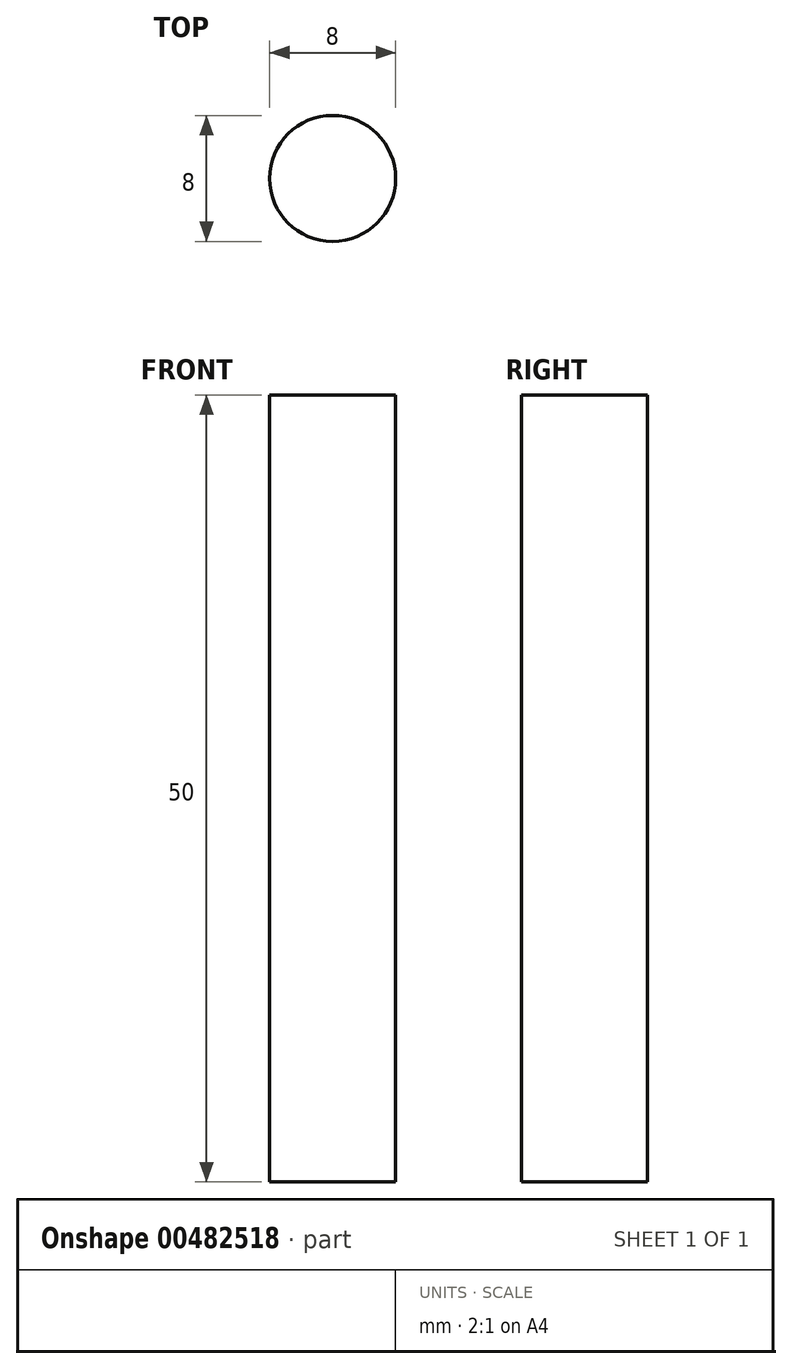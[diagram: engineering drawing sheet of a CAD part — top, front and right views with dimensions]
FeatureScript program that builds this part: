
annotation { "Feature Type Name" : "Feature", "Feature Type Description" : "" }
export const myFeature = defineFeature(function(context is Context, id is Id, definition is map)
    precondition{}
    {
        {
            var Q0;
            Q0=qCreatedBy(makeId("Top.planeOp"),FACE);
            var sketch = newSketch(context, id + "F0", { "sketchPlane" : qUnion([Q0])});
            skCircle(sketch, "E0", {"center": v(0, 0) * mm, "radius": 4 * mm});
            skSolve(sketch);
        }
        {
            var Q0;
            Q0 = qSketchRegion(id + "F0", true);
            extrude(context, id + "F1", {"entities" : qUnion([Q0]), "depth" : 50 * mm, "offsetDistance" : 25 * mm});
        }
    });
